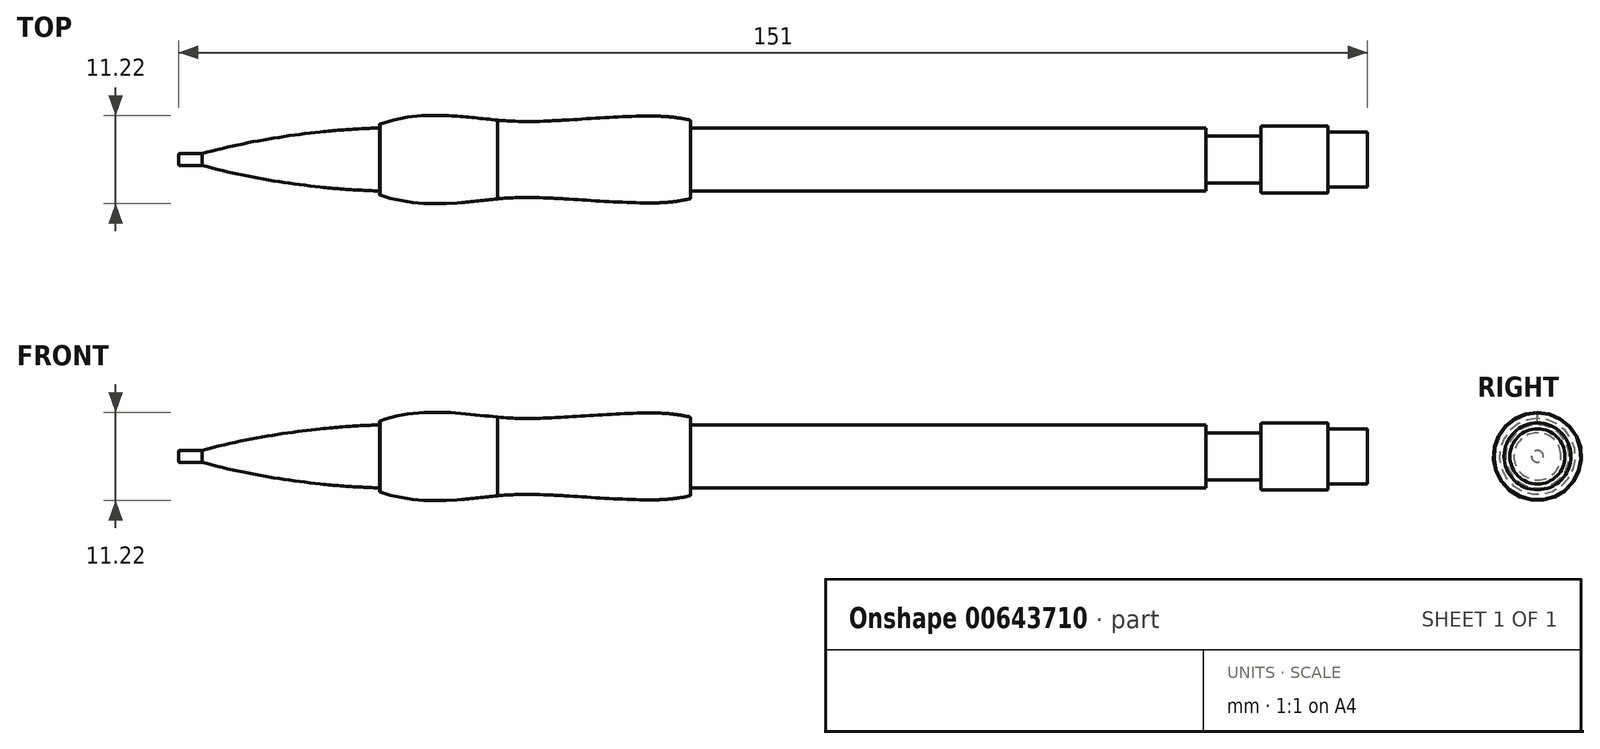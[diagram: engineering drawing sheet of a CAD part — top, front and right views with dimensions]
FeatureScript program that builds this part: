
annotation { "Feature Type Name" : "Feature", "Feature Type Description" : "" }
export const myFeature = defineFeature(function(context is Context, id is Id, definition is map)
    precondition{}
    {
        {
            var Q0;
            Q0=qCreatedBy(makeId("Front.planeOp"),FACE);
            var sketch = newSketch(context, id + "F0", { "sketchPlane" : qUnion([Q0])});
            skLineSegment(sketch, "E0", {"start": v(-73.47, 0) * mm, "end": v(77.53, 0) * mm});
            skLineSegment(sketch, "E1.bottom", {"start": v(77.53, 0) * mm, "end": v(72.53, 0) * mm});
            skLineSegment(sketch, "E1.top", {"start": v(77.53, 3.5) * mm, "end": v(72.53, 3.5) * mm});
            skLineSegment(sketch, "E1.left", {"start": v(77.53, 0) * mm, "end": v(77.53, 3.5) * mm});
            skLineSegment(sketch, "E1.right", {"start": v(72.53, 0) * mm, "end": v(72.53, 3.5) * mm});
            skLineSegment(sketch, "E2.bottom", {"start": v(72.53, 0) * mm, "end": v(64.03, 0) * mm});
            skLineSegment(sketch, "E2.top", {"start": v(72.53, 4.25) * mm, "end": v(64.03, 4.25) * mm});
            skLineSegment(sketch, "E2.left", {"start": v(72.53, 0) * mm, "end": v(72.53, 4.25) * mm});
            skLineSegment(sketch, "E2.right", {"start": v(64.03, 0) * mm, "end": v(64.03, 4.25) * mm});
            skLineSegment(sketch, "E3.bottom", {"start": v(64.03, 0) * mm, "end": v(57.03, 0) * mm});
            skLineSegment(sketch, "E3.top", {"start": v(64.03, 3) * mm, "end": v(57.03, 3) * mm});
            skLineSegment(sketch, "E3.left", {"start": v(64.03, 0) * mm, "end": v(64.03, 3) * mm});
            skLineSegment(sketch, "E3.right", {"start": v(57.03, 0) * mm, "end": v(57.03, 3) * mm});
            skLineSegment(sketch, "E4.bottom", {"start": v(57.03, 0) * mm, "end": v(-8.47, 0) * mm});
            skLineSegment(sketch, "E4.top", {"start": v(57.03, 4) * mm, "end": v(-8.47, 4) * mm});
            skLineSegment(sketch, "E4.left", {"start": v(57.03, 0) * mm, "end": v(57.03, 4) * mm});
            skLineSegment(sketch, "E4.right", {"start": v(-8.47, 0) * mm, "end": v(-8.47, 4) * mm});
            skLineSegment(sketch, "E5.bottom", {"start": v(-73.47, 0) * mm, "end": v(-70.47, 0) * mm});
            skLineSegment(sketch, "E5.top", {"start": v(-73.47, 0.75) * mm, "end": v(-70.47, 0.75) * mm});
            skLineSegment(sketch, "E5.left", {"start": v(-73.47, 0) * mm, "end": v(-73.47, 0.75) * mm});
            skLineSegment(sketch, "E5.right", {"start": v(-70.47, 0) * mm, "end": v(-70.47, 0.75) * mm});
            skLineSegment(sketch, "E6", {"start": v(-8.47, 0) * mm, "end": v(-8.47, 5) * mm});
            skLineSegment(sketch, "E7", {"start": v(-12.47, 0) * mm, "end": v(-12.47, 5.5) * mm});
            skLineSegment(sketch, "E8", {"start": v(-24.47, 0) * mm, "end": v(-24.47, 5) * mm});
            skLineSegment(sketch, "E9", {"start": v(-32.97, 0) * mm, "end": v(-32.97, 5) * mm});
            skLineSegment(sketch, "E10", {"start": v(-47.97, 0) * mm, "end": v(-47.97, 4.5) * mm});
            skLineSegment(sketch, "E11", {"start": v(-47.97, 0) * mm, "end": v(-47.97, 4) * mm});
            skLineSegment(sketch, "E12", {"start": v(-55.47, 0) * mm, "end": v(-55.47, 3.5) * mm});
            skFitSpline(sketch, "E13", {"points": [v(-70.47, 0.75) * mm, v(-55.47, 3.5) * mm, v(-47.97, 4) * mm], "startDerivative": vector(27.32, 7.64) * mm, "endDerivative": vector(16.67, 0.5) * mm});
            skFitSpline(sketch, "E14", {"points": [v(-47.97, 4.5) * mm, v(-32.97, 5) * mm, v(-24.47, 5) * mm, v(-12.47, 5.5) * mm, v(-8.47, 5) * mm], "startDerivative": vector(51.27, 17.94) * mm, "endDerivative": vector(20.26, -4.15) * mm});
            skSolve(sketch);
        }
        {
            var Q0;
            Q0 = qSketchRegion(id + "F0", true);
            var Q1;
            Q1=sQuery(id+"F0.wireOp",EDGE,"E0");
            revolve(context, id + "F1", {"entities" : qUnion([Q0]), "axis" : qUnion([Q1]), "revolveType" : RevolveType.FULL});
        }
        {
            var Q0;
            Q0=makeQuery(id+"F1.opRevolve","SWEPT_EDGE",EDGE,{"disambiguationData":[OSD([sQuery(id+"F0.wireOp",EDGE,"E5.top"),sQuery(id+"F0.wireOp",EDGE,"E5.left")])]});
            var Q1;
            Q1=makeQuery(id+"F1.opRevolve","SWEPT_EDGE",EDGE,{"disambiguationData":[OSD([sQuery(id+"F0.wireOp",EDGE,"E10"),sQuery(id+"F0.wireOp",EDGE,"E14")])]});
            var Q2;
            Q2=makeQuery(id+"F1.opRevolve","SWEPT_EDGE",EDGE,{"disambiguationData":[OSD([sQuery(id+"F0.wireOp",EDGE,"E6"),sQuery(id+"F0.wireOp",EDGE,"E14")])]});
            var Q3;
            Q3=makeQuery(id+"F1.opRevolve","SWEPT_EDGE",EDGE,{"disambiguationData":[OSD([sQuery(id+"F0.wireOp",EDGE,"E2.top"),sQuery(id+"F0.wireOp",EDGE,"E2.left")])]});
            var Q4;
            Q4=makeQuery(id+"F1.opRevolve","SWEPT_EDGE",EDGE,{"disambiguationData":[OSD([sQuery(id+"F0.wireOp",EDGE,"E1.top"),sQuery(id+"F0.wireOp",EDGE,"E1.left")])]});
            var Q5;
            Q5=makeQuery(id+"F1.opRevolve","SWEPT_EDGE",EDGE,{"disambiguationData":[OSD([sQuery(id+"F0.wireOp",EDGE,"E2.top"),sQuery(id+"F0.wireOp",EDGE,"E2.right")])]});
            fillet(context, id + "F2", {"entities" : qUnion([Q0, Q1, Q2, Q3, Q4, Q5]), "radius" : 0.1 * mm, "allowEdgeOverflow" : false});
        }
    });
